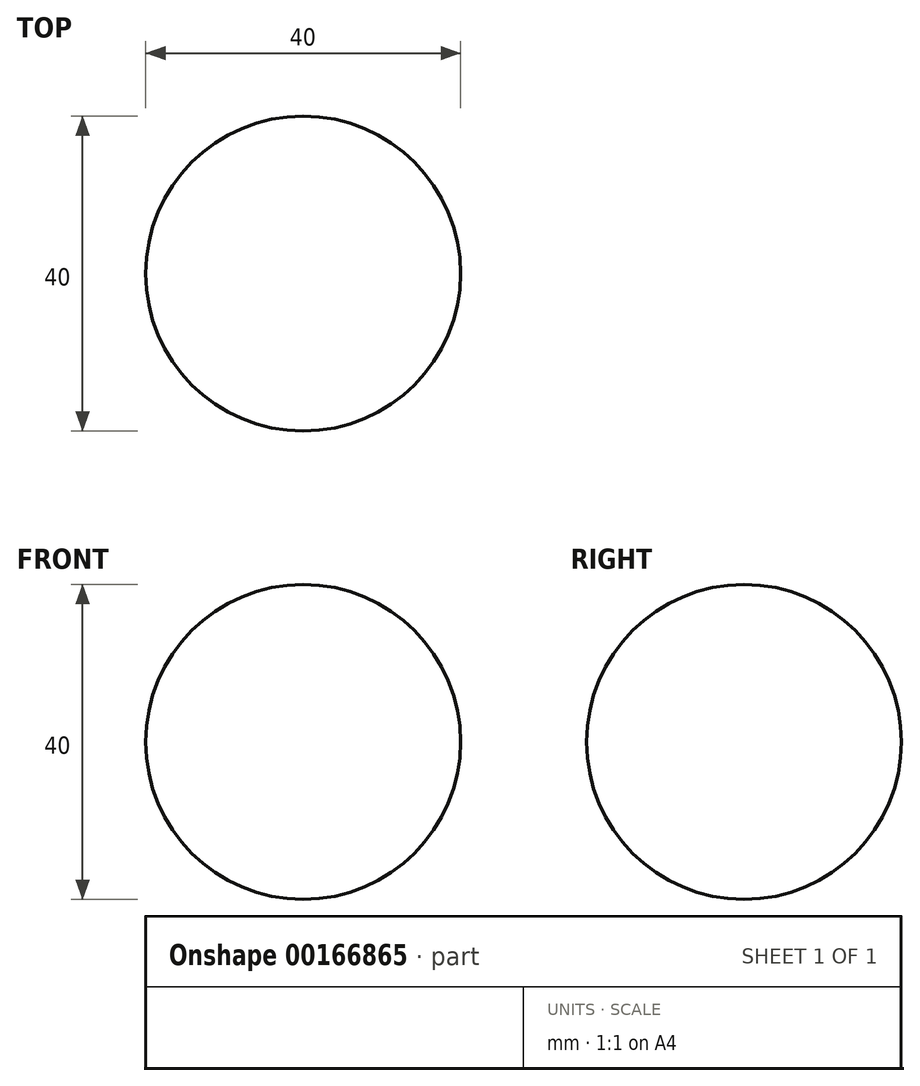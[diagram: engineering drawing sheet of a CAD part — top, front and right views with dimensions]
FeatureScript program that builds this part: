
annotation { "Feature Type Name" : "Feature", "Feature Type Description" : "" }
export const myFeature = defineFeature(function(context is Context, id is Id, definition is map)
    precondition{}
    {
        {
            var Q0;
            Q0=qCreatedBy(makeId("Top.planeOp"),FACE);
            var sketch = newSketch(context, id + "F0", { "sketchPlane" : qUnion([Q0])});
            skArc(sketch, "E0", {"start": v(20, 0) * mm, "mid": v(0, 20) * mm, "end": v(-20, 0) * mm});
            skLineSegment(sketch, "E1", {"start": v(-20, 0) * mm, "end": v(20, 0) * mm});
            skSolve(sketch);
        }
        {
            var Q0;
            Q0=makeQuery(id+"F0.imprint","IMPRINT",FACE,{"disambiguationData":[TD([[makeQuery(id+"F0.imprint","IMPRINT",EDGE,{"derivedFrom":sQuery(id+"F0.wireOp",EDGE,"E0")}),1.0]])]});
            var Q1;
            Q1=sQuery(id+"F0.wireOp",EDGE,"E1");
            revolve(context, id + "F1", {"entities" : qUnion([Q0]), "axis" : qUnion([Q1]), "revolveType" : RevolveType.FULL});
        }
    });
